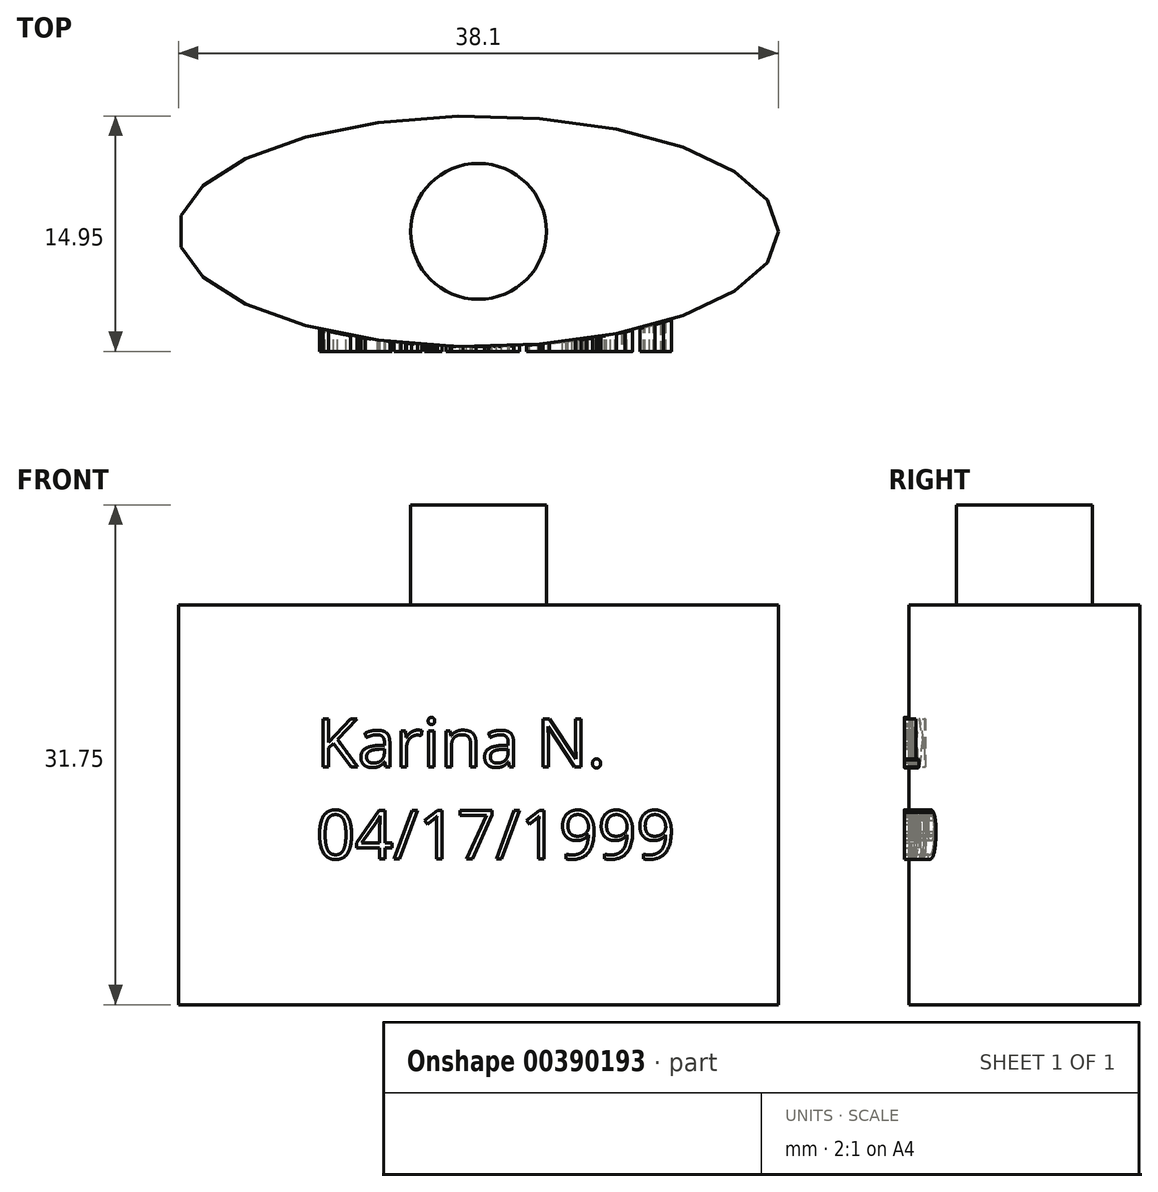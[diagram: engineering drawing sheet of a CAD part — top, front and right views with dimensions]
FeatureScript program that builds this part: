
annotation { "Feature Type Name" : "Feature", "Feature Type Description" : "" }
export const myFeature = defineFeature(function(context is Context, id is Id, definition is map)
    precondition{}
    {
        {
            var Q0;
            Q0=qCreatedBy(makeId("Top.planeOp"),FACE);
            var sketch = newSketch(context, id + "F0", { "sketchPlane" : qUnion([Q0])});
            skEllipse(sketch, "E0", {"center": v(0, 0) * mm, "majorRadius": 19.05 * mm, "minorRadius": 7.33 * mm, "majorAxis": v(1, 0)});
            skSolve(sketch);
        }
        {
            var Q0;
            Q0=makeQuery(id+"F0.imprint","IMPRINT",FACE,{"disambiguationData":[TD([[makeQuery(id+"F0.imprint","IMPRINT",EDGE,{"derivedFrom":sQuery(id+"F0.wireOp",EDGE,"E0")}),1.0]])]});
            extrude(context, id + "F1", {"entities" : qUnion([Q0]), "depth" : 25.4 * mm});
        }
        {
            var Q0;
            Q0=makeQuery(id+"F1.opExtrude","CAP_FACE",FACE,{"disambiguationData":[OSD([sQuery(id+"F0.wireOp",EDGE,"E0")])],"isStart":false});
            var sketch = newSketch(context, id + "F2", { "sketchPlane" : qUnion([Q0])});
            skCircle(sketch, "E1", {"center": v(0, 0) * mm, "radius": 4.32 * mm});
            skSolve(sketch);
        }
        {
            var Q0;
            Q0=makeQuery(id+"F2.imprint","IMPRINT",FACE,{"disambiguationData":[TD([[makeQuery(id+"F2.imprint","IMPRINT",EDGE,{"derivedFrom":sQuery(id+"F2.wireOp",EDGE,"E1")}),1.0]])]});
            extrude(context, id + "F3", {"entities" : qUnion([Q0]), "operationType" : NewBodyOperationType.ADD, "depth" : 6.35 * mm});
        }
        {
            var Q0;
            Q0=qCreatedBy(makeId("Front.planeOp"),FACE);
            var sketch = newSketch(context, id + "F4", { "sketchPlane" : qUnion([Q0])});
            skText(sketch, "E2", { "text": "Karina N.\n04/17/1999", "fontName": "OpenSans-Regular.ttf"});
            const initialGuessF4  = {"E2": [-0.0103, 0.0151, 1, 0, 0.00309]};
            skSetInitialGuess(sketch, initialGuessF4);
            skSolve(sketch);
        }
        {
            var Q0;
            Q0 = qSketchRegion(id + "F4", true);
            extrude(context, id + "F5", {"entities" : qUnion([Q0]), "operationType" : NewBodyOperationType.ADD, "depth" : 7.62 * mm});
        }
    });
